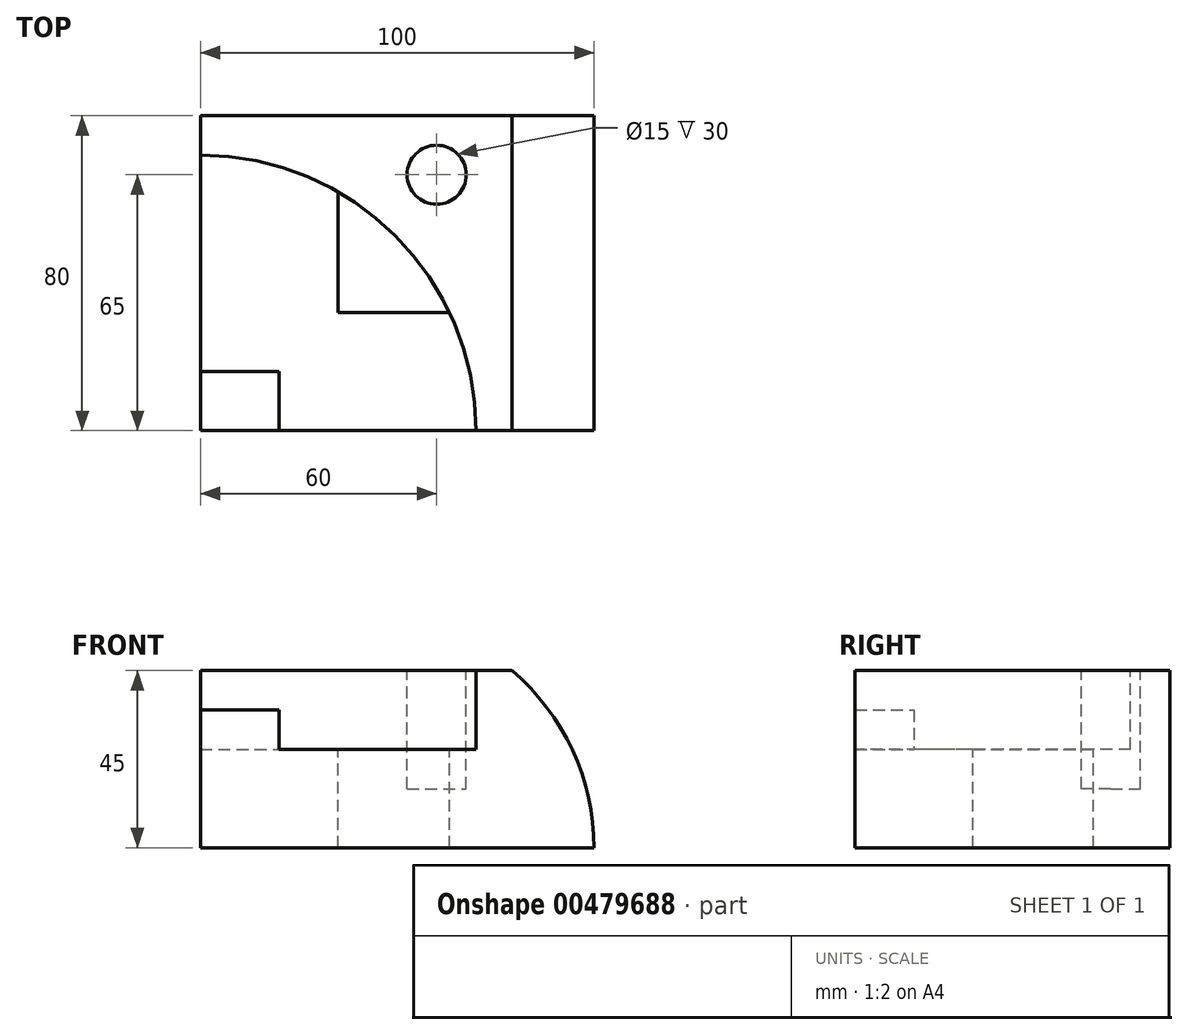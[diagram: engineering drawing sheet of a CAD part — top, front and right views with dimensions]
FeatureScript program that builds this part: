
annotation { "Feature Type Name" : "Feature", "Feature Type Description" : "" }
export const myFeature = defineFeature(function(context is Context, id is Id, definition is map)
    precondition{}
    {
        {
            var Q0;
            Q0=qCreatedBy(makeId("Top.planeOp"),FACE);
            var sketch = newSketch(context, id + "F0", { "sketchPlane" : qUnion([Q0])});
            skLineSegment(sketch, "E0.bottom", {"start": v(0, 0) * mm, "end": v(100, 0) * mm});
            skLineSegment(sketch, "E0.top", {"start": v(0, 80) * mm, "end": v(100, 80) * mm});
            skLineSegment(sketch, "E0.left", {"start": v(0, 0) * mm, "end": v(0, 80) * mm});
            skLineSegment(sketch, "E0.right", {"start": v(100, 0) * mm, "end": v(100, 80) * mm});
            skSolve(sketch);
        }
        {
            var Q0;
            Q0=qSketchRegion(id+"F0",true);
            extrude(context, id + "F1", {"entities" : qUnion([Q0]), "depth" : 45 * mm});
        }
        {
            var Q0;
            Q0=makeQuery(id+"F1.opExtrude","CAP_FACE",FACE,{"disambiguationData":[OSD([sQuery(id+"F0.wireOp",EDGE,"E0.bottom"),sQuery(id+"F0.wireOp",EDGE,"E0.top"),sQuery(id+"F0.wireOp",EDGE,"E0.left"),sQuery(id+"F0.wireOp",EDGE,"E0.right")])],"isStart":true});
            cPlane(context, id + "F2", {"entities" : qUnion([Q0]), "cplaneType" : CPlaneType.OFFSET, "offset" : 25 * mm, "oppositeDirection" : true, "width" : 150 * mm, "height" : 150 * mm});
        }
        {
            var Q0;
            Q0=qCreatedBy(id+"F2.planeOp",FACE);
            cPlane(context, id + "F3", {"entities" : qUnion([Q0]), "cplaneType" : CPlaneType.OFFSET, "offset" : 10 * mm, "oppositeDirection" : true, "width" : 150 * mm, "height" : 150 * mm});
        }
        {
            var Q0;
            Q0=makeQuery(id+"F1.opExtrude","CAP_FACE",FACE,{"disambiguationData":[OSD([sQuery(id+"F0.wireOp",EDGE,"E0.bottom"),sQuery(id+"F0.wireOp",EDGE,"E0.top"),sQuery(id+"F0.wireOp",EDGE,"E0.left"),sQuery(id+"F0.wireOp",EDGE,"E0.right")])],"isStart":true});
            cPlane(context, id + "F4", {"entities" : qUnion([Q0]), "cplaneType" : CPlaneType.OFFSET, "offset" : 15 * mm, "oppositeDirection" : true, "width" : 150 * mm, "height" : 150 * mm});
        }
        {
            var Q0;
            Q0=makeQuery(id+"F1.opExtrude","CAP_FACE",FACE,{"disambiguationData":[OSD([sQuery(id+"F0.wireOp",EDGE,"E0.bottom"),sQuery(id+"F0.wireOp",EDGE,"E0.top"),sQuery(id+"F0.wireOp",EDGE,"E0.left"),sQuery(id+"F0.wireOp",EDGE,"E0.right")])],"isStart":false});
            var sketch = newSketch(context, id + "F5", { "sketchPlane" : qUnion([Q0])});
            skCircle(sketch, "E1", {"center": v(60, 65) * mm, "radius": 7.5 * mm});
            skSolve(sketch);
        }
        {
            var Q0;
            Q0=qSketchRegion(id+"F5",true);
            var Q1;
            Q1=qCreatedBy(id+"F4.planeOp",FACE);
            extrude(context, id + "F6", {"entities" : qUnion([Q0]), "operationType" : NewBodyOperationType.REMOVE, "endBound" : BoundingType.UP_TO_SURFACE, "oppositeDirection" : true, "endBoundEntityFace" : qUnion([Q1]), "depth" : 25 * mm});
        }
        {
            var Q0;
            Q0=makeQuery(id+"F1.opExtrude","SWEPT_FACE",FACE,{"disambiguationData":[OSD([sQuery(id+"F0.wireOp",EDGE,"E0.bottom")])]});
            var sketch = newSketch(context, id + "F7", { "sketchPlane" : qUnion([Q0])});
            skCircle(sketch, "E2", {"center": v(41.1, 0) * mm, "radius": 58.9 * mm});
            skSolve(sketch);
        }
        {
            var Q0;
            {var subQ1=sQuery(id+"F0.wireOp",EDGE,"E0.bottom");var subQ2=makeQuery(id+"F1.opExtrude","SWEPT_EDGE",EDGE,{"disambiguationData":[OSD([subQ1,sQuery(id+"F0.wireOp",EDGE,"E0.right")])]});Q0=makeQuery(id+"F7.imprint","IMPRINT",FACE,{"disambiguationData":[TD([[makeQuery(id+"F7.imprint","IMPRINT",EDGE,{"derivedFrom":subQ2}),-1.0]])]});}
            extrude(context, id + "F8", {"entities" : qUnion([Q0]), "operationType" : NewBodyOperationType.REMOVE, "endBound" : BoundingType.THROUGH_ALL, "oppositeDirection" : true, "depth" : 25 * mm});
        }
        {
            var Q0;
            Q0=makeQuery(id+"F1.opExtrude","CAP_FACE",FACE,{"disambiguationData":[OSD([sQuery(id+"F0.wireOp",EDGE,"E0.bottom"),sQuery(id+"F0.wireOp",EDGE,"E0.top"),sQuery(id+"F0.wireOp",EDGE,"E0.left"),sQuery(id+"F0.wireOp",EDGE,"E0.right")])],"isStart":false});
            var sketch = newSketch(context, id + "F9", { "sketchPlane" : qUnion([Q0])});
            skCircle(sketch, "E3", {"center": v(0, 0) * mm, "radius": 70 * mm});
            skSolve(sketch);
        }
        {
            var Q0;
            Q0=qSketchRegion(id+"F9",true);
            var Q1;
            Q1=qCreatedBy(id+"F2.planeOp",FACE);
            extrude(context, id + "F10", {"entities" : qUnion([Q0]), "operationType" : NewBodyOperationType.REMOVE, "endBound" : BoundingType.UP_TO_SURFACE, "oppositeDirection" : true, "endBoundEntityFace" : qUnion([Q1]), "depth" : 25 * mm});
        }
        {
            var Q0;
            Q0=makeQuery(id+"F10.boolean.opBoolean","COPY",FACE,{"derivedFrom":makeQuery(id+"F10.opExtrude","CAP_FACE",FACE,{"disambiguationData":[OSD([sQuery(id+"F9.wireOp",EDGE,"E3")])],"isStart":false})});
            var sketch = newSketch(context, id + "F11", { "sketchPlane" : qUnion([Q0])});
            skLineSegment(sketch, "E4.bottom", {"start": v(0, 0) * mm, "end": v(20, 0) * mm});
            skLineSegment(sketch, "E4.top", {"start": v(0, 15) * mm, "end": v(20, 15) * mm});
            skLineSegment(sketch, "E4.left", {"start": v(0, 0) * mm, "end": v(0, 15) * mm});
            skLineSegment(sketch, "E4.right", {"start": v(20, 0) * mm, "end": v(20, 15) * mm});
            skSolve(sketch);
        }
        {
            var Q0;
            Q0=qSketchRegion(id+"F11",true);
            var Q1;
            Q1=qCreatedBy(id+"F3.planeOp",FACE);
            extrude(context, id + "F12", {"entities" : qUnion([Q0]), "operationType" : NewBodyOperationType.ADD, "endBound" : BoundingType.UP_TO_SURFACE, "endBoundEntityFace" : qUnion([Q1]), "depth" : 25 * mm});
        }
        {
            var Q0;
            Q0=makeQuery(id+"F10.boolean.opBoolean","COPY",FACE,{"derivedFrom":makeQuery(id+"F10.opExtrude","CAP_FACE",FACE,{"disambiguationData":[OSD([sQuery(id+"F9.wireOp",EDGE,"E3")])],"isStart":false})});
            var sketch = newSketch(context, id + "F13", { "sketchPlane" : qUnion([Q0])});
            skLineSegment(sketch, "E5", {"start": v(63.25, 30) * mm, "end": v(35, 30) * mm});
            skLineSegment(sketch, "E6", {"start": v(35, 30) * mm, "end": v(35, 60.62) * mm});
            skSolve(sketch);
        }
        {
            var Q0;
            Q0=qSketchRegion(id+"F13",true);
            var Q1;
            {var subQ0=sQuery(id+"F13.wireOp",EDGE,"E5");Q1=makeQuery(id+"F13.imprint","IMPRINT",FACE,{"disambiguationData":[TD([[makeQuery(id+"F13.imprint","IMPRINT",EDGE,{"derivedFrom":subQ0}),-1.0]])]});}
            extrude(context, id + "F14", {"entities" : qUnion([Q0, Q1]), "operationType" : NewBodyOperationType.REMOVE, "endBound" : BoundingType.THROUGH_ALL, "oppositeDirection" : true, "depth" : 25 * mm});
        }
    });
